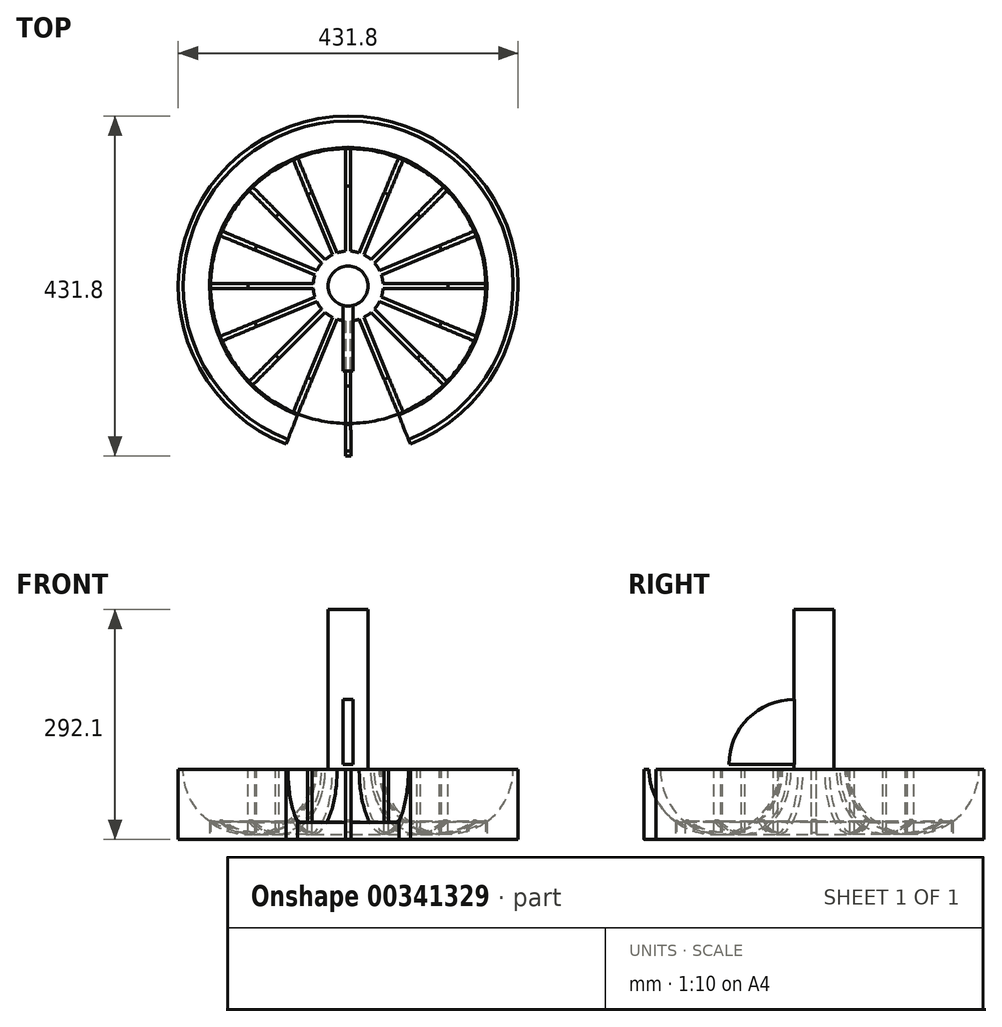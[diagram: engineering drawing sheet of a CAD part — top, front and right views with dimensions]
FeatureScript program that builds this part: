
annotation { "Feature Type Name" : "Feature", "Feature Type Description" : "" }
export const myFeature = defineFeature(function(context is Context, id is Id, definition is map)
    precondition{}
    {
        {
            var Q0;
            Q0=qCreatedBy(makeId("Front.planeOp"),FACE);
            var sketch = newSketch(context, id + "F0", { "sketchPlane" : qUnion([Q0])});
            skLineSegment(sketch, "E0.bottom", {"start": v(0, 0) * mm, "end": v(25.4, 0) * mm});
            skLineSegment(sketch, "E0.top", {"start": v(0, 292.1) * mm, "end": v(25.4, 292.1) * mm});
            skLineSegment(sketch, "E0.left", {"start": v(0, 0) * mm, "end": v(0, 292.1) * mm});
            skLineSegment(sketch, "E0.right", {"start": v(25.4, 88.9) * mm, "end": v(25.4, 292.1) * mm});
            skLineSegment(sketch, "E1.bottom", {"start": v(38.1, 0) * mm, "end": v(215.9, 0) * mm});
            skLineSegment(sketch, "E1.top", {"start": v(38.1, 88.9) * mm, "end": v(44.45, 88.9) * mm});
            skLineSegment(sketch, "E1.right", {"start": v(215.9, 0) * mm, "end": v(215.9, 88.9) * mm});
            skArc(sketch, "E2", {"start": v(209.55, 88.9) * mm, "mid": v(127, 6.35) * mm, "end": v(44.45, 88.9) * mm});
            skLineSegment(sketch, "E3", {"start": v(38.1, 88.9) * mm, "end": v(25.4, 88.9) * mm});
            skLineSegment(sketch, "E4", {"start": v(38.1, 0) * mm, "end": v(25.4, 0) * mm});
            skLineSegment(sketch, "E5.trimOffspring", {"start": v(209.55, 88.9) * mm, "end": v(215.9, 88.9) * mm});
            skSolve(sketch);
        }
        {
            var Q0;
            Q0=makeQuery(id+"F0.imprint","IMPRINT",FACE,{"disambiguationData":[TD([[makeQuery(id+"F0.imprint","IMPRINT",EDGE,{"derivedFrom":sQuery(id+"F0.wireOp",EDGE,"E0.bottom")}),1.0]])]});
            var Q1;
            Q1=sQuery(id+"F0.wireOp",EDGE,"E0.left");
            revolve(context, id + "F1", {"entities" : qUnion([Q0]), "axis" : qUnion([Q1]), "revolveType" : RevolveType.FULL});
        }
        {
            var Q0;
            Q0=qCreatedBy(makeId("Front.planeOp"),FACE);
            var sketch = newSketch(context, id + "F2", { "sketchPlane" : qUnion([Q0])});
            skLineSegment(sketch, "E6.bottom", {"start": v(0, 0) * mm, "end": v(127, 0) * mm, "construction": true});
            skLineSegment(sketch, "E6.top", {"start": v(0, 88.9) * mm, "end": v(127, 88.9) * mm, "construction": true});
            skLineSegment(sketch, "E6.left", {"start": v(0, 0) * mm, "end": v(0, 88.9) * mm, "construction": true});
            skLineSegment(sketch, "E6.right", {"start": v(127, 0) * mm, "end": v(127, 88.9) * mm, "construction": true});
            skArc(sketch, "E7", {"start": v(207.01, 88.9) * mm, "mid": v(127, 8.89) * mm, "end": v(46.99, 88.9) * mm});
            skArc(sketch, "E8", {"start": v(41.9, 88.9) * mm, "mid": v(127, 3.8) * mm, "end": v(212.1, 88.9) * mm});
            skLineSegment(sketch, "E9", {"start": v(41.9, 88.9) * mm, "end": v(46.99, 88.9) * mm});
            skLineSegment(sketch, "E10", {"start": v(207.01, 88.9) * mm, "end": v(212.1, 88.9) * mm});
            skLineSegment(sketch, "E11", {"start": v(46.99, 88.9) * mm, "end": v(127, 88.9) * mm});
            skLineSegment(sketch, "E12", {"start": v(127, 8.89) * mm, "end": v(127, 88.9) * mm});
            skSolve(sketch);
        }
        {
            var Q0;
            Q0 = qSketchRegion(id + "F2", true);
            extrude(context, id + "F3", {"entities" : qUnion([Q0]), "operationType" : NewBodyOperationType.ADD, "endBound" : BoundingType.SYMMETRIC, "depth" : 6.35 * mm});
        }
        {
            var Q0;
            Q0=makeQuery(id+"F1.opRevolve","SWEPT_BODY",BODY,{"disambiguationData":[OSD([sQuery(id+"F0.wireOp",EDGE,"E0.bottom"),sQuery(id+"F0.wireOp",EDGE,"E0.top"),sQuery(id+"F0.wireOp",EDGE,"E0.left"),sQuery(id+"F0.wireOp",EDGE,"E0.right"),sQuery(id+"F0.wireOp",EDGE,"E1.bottom"),sQuery(id+"F0.wireOp",EDGE,"E1.top"),sQuery(id+"F0.wireOp",EDGE,"E1.right"),sQuery(id+"F0.wireOp",EDGE,"E2"),sQuery(id+"F0.wireOp",EDGE,"E3"),sQuery(id+"F0.wireOp",EDGE,"E4"),sQuery(id+"F0.wireOp",EDGE,"E5.trimOffspring")])]});
            var Q1;
            Q1=makeQuery(id+"F1.opRevolve","SWEPT_FACE",FACE,{"disambiguationData":[OSD([sQuery(id+"F0.wireOp",EDGE,"E0.right")])]});
            circularPattern(context, id + "F4", {"entities" : qUnion([Q0]), "axis" : qUnion([Q1]), "angle" : 360 * degree, "instanceCount" : 16, "equalSpace" : true});
        }
        {
            var Q0;
            Q0=qCreatedBy(makeId("Right.planeOp"),FACE);
            var sketch = newSketch(context, id + "F5", { "sketchPlane" : qUnion([Q0])});
            skLineSegment(sketch, "E13", {"start": v(0, 0) * mm, "end": v(0, 232.3) * mm, "construction": true});
            skLineSegment(sketch, "E14", {"start": v(0, 232.3) * mm, "end": v(0, 0) * mm, "construction": true});
            skLineSegment(sketch, "E15", {"start": v(-25.4, 254.95) * mm, "end": v(-25.4, -56.78) * mm, "construction": true});
            skLineSegment(sketch, "E16", {"start": v(-25.4, 95.25) * mm, "end": v(-107.95, 95.25) * mm});
            skArc(sketch, "E17", {"start": v(-107.95, 95.25) * mm, "mid": v(-83.77, 153.62) * mm, "end": v(-25.4, 177.8) * mm});
            skLineSegment(sketch, "E18.bottom", {"start": v(-25.4, 95.25) * mm, "end": v(-12.7, 95.25) * mm});
            skLineSegment(sketch, "E18.top", {"start": v(-25.4, 177.8) * mm, "end": v(-12.7, 177.8) * mm});
            skLineSegment(sketch, "E18.left", {"start": v(-25.4, 95.25) * mm, "end": v(-25.4, 177.8) * mm});
            skLineSegment(sketch, "E18.right", {"start": v(-12.7, 95.25) * mm, "end": v(-12.7, 177.8) * mm});
            skSolve(sketch);
        }
        {
            var Q0;
            Q0 = qSketchRegion(id + "F5", true);
            extrude(context, id + "F6", {"entities" : qUnion([Q0]), "endBound" : BoundingType.SYMMETRIC, "depth" : 12.7 * mm});
        }
        {
            var Q0;
            Q0=makeQuery(id+"F4.opPattern","COPY",BODY,{"derivedFrom":makeQuery(id+"F1.opRevolve","SWEPT_BODY",BODY,{"disambiguationData":[OSD([sQuery(id+"F0.wireOp",EDGE,"E0.bottom"),sQuery(id+"F0.wireOp",EDGE,"E0.top"),sQuery(id+"F0.wireOp",EDGE,"E0.left"),sQuery(id+"F0.wireOp",EDGE,"E0.right"),sQuery(id+"F0.wireOp",EDGE,"E1.bottom"),sQuery(id+"F0.wireOp",EDGE,"E1.top"),sQuery(id+"F0.wireOp",EDGE,"E1.right"),sQuery(id+"F0.wireOp",EDGE,"E2"),sQuery(id+"F0.wireOp",EDGE,"E3"),sQuery(id+"F0.wireOp",EDGE,"E4"),sQuery(id+"F0.wireOp",EDGE,"E5.trimOffspring")])]}),"instanceName":"1"});
            var Q1;
            Q1=makeQuery(id+"F4.opPattern","COPY",BODY,{"derivedFrom":makeQuery(id+"F1.opRevolve","SWEPT_BODY",BODY,{"disambiguationData":[OSD([sQuery(id+"F0.wireOp",EDGE,"E0.bottom"),sQuery(id+"F0.wireOp",EDGE,"E0.top"),sQuery(id+"F0.wireOp",EDGE,"E0.left"),sQuery(id+"F0.wireOp",EDGE,"E0.right"),sQuery(id+"F0.wireOp",EDGE,"E1.bottom"),sQuery(id+"F0.wireOp",EDGE,"E1.top"),sQuery(id+"F0.wireOp",EDGE,"E1.right"),sQuery(id+"F0.wireOp",EDGE,"E2"),sQuery(id+"F0.wireOp",EDGE,"E3"),sQuery(id+"F0.wireOp",EDGE,"E4"),sQuery(id+"F0.wireOp",EDGE,"E5.trimOffspring")])]}),"instanceName":"2"});
            var Q2;
            Q2=makeQuery(id+"F4.opPattern","COPY",BODY,{"derivedFrom":makeQuery(id+"F1.opRevolve","SWEPT_BODY",BODY,{"disambiguationData":[OSD([sQuery(id+"F0.wireOp",EDGE,"E0.bottom"),sQuery(id+"F0.wireOp",EDGE,"E0.top"),sQuery(id+"F0.wireOp",EDGE,"E0.left"),sQuery(id+"F0.wireOp",EDGE,"E0.right"),sQuery(id+"F0.wireOp",EDGE,"E1.bottom"),sQuery(id+"F0.wireOp",EDGE,"E1.top"),sQuery(id+"F0.wireOp",EDGE,"E1.right"),sQuery(id+"F0.wireOp",EDGE,"E2"),sQuery(id+"F0.wireOp",EDGE,"E3"),sQuery(id+"F0.wireOp",EDGE,"E4"),sQuery(id+"F0.wireOp",EDGE,"E5.trimOffspring")])]}),"instanceName":"3"});
            var Q3;
            Q3=makeQuery(id+"F4.opPattern","COPY",BODY,{"derivedFrom":makeQuery(id+"F1.opRevolve","SWEPT_BODY",BODY,{"disambiguationData":[OSD([sQuery(id+"F0.wireOp",EDGE,"E0.bottom"),sQuery(id+"F0.wireOp",EDGE,"E0.top"),sQuery(id+"F0.wireOp",EDGE,"E0.left"),sQuery(id+"F0.wireOp",EDGE,"E0.right"),sQuery(id+"F0.wireOp",EDGE,"E1.bottom"),sQuery(id+"F0.wireOp",EDGE,"E1.top"),sQuery(id+"F0.wireOp",EDGE,"E1.right"),sQuery(id+"F0.wireOp",EDGE,"E2"),sQuery(id+"F0.wireOp",EDGE,"E3"),sQuery(id+"F0.wireOp",EDGE,"E4"),sQuery(id+"F0.wireOp",EDGE,"E5.trimOffspring")])]}),"instanceName":"7"});
            var Q4;
            Q4=makeQuery(id+"F4.opPattern","COPY",BODY,{"derivedFrom":makeQuery(id+"F1.opRevolve","SWEPT_BODY",BODY,{"disambiguationData":[OSD([sQuery(id+"F0.wireOp",EDGE,"E0.bottom"),sQuery(id+"F0.wireOp",EDGE,"E0.top"),sQuery(id+"F0.wireOp",EDGE,"E0.left"),sQuery(id+"F0.wireOp",EDGE,"E0.right"),sQuery(id+"F0.wireOp",EDGE,"E1.bottom"),sQuery(id+"F0.wireOp",EDGE,"E1.top"),sQuery(id+"F0.wireOp",EDGE,"E1.right"),sQuery(id+"F0.wireOp",EDGE,"E2"),sQuery(id+"F0.wireOp",EDGE,"E3"),sQuery(id+"F0.wireOp",EDGE,"E4"),sQuery(id+"F0.wireOp",EDGE,"E5.trimOffspring")])]}),"instanceName":"4"});
            var Q5;
            Q5=makeQuery(id+"F4.opPattern","COPY",BODY,{"derivedFrom":makeQuery(id+"F1.opRevolve","SWEPT_BODY",BODY,{"disambiguationData":[OSD([sQuery(id+"F0.wireOp",EDGE,"E0.bottom"),sQuery(id+"F0.wireOp",EDGE,"E0.top"),sQuery(id+"F0.wireOp",EDGE,"E0.left"),sQuery(id+"F0.wireOp",EDGE,"E0.right"),sQuery(id+"F0.wireOp",EDGE,"E1.bottom"),sQuery(id+"F0.wireOp",EDGE,"E1.top"),sQuery(id+"F0.wireOp",EDGE,"E1.right"),sQuery(id+"F0.wireOp",EDGE,"E2"),sQuery(id+"F0.wireOp",EDGE,"E3"),sQuery(id+"F0.wireOp",EDGE,"E4"),sQuery(id+"F0.wireOp",EDGE,"E5.trimOffspring")])]}),"instanceName":"5"});
            var Q6;
            Q6=makeQuery(id+"F4.opPattern","COPY",BODY,{"derivedFrom":makeQuery(id+"F1.opRevolve","SWEPT_BODY",BODY,{"disambiguationData":[OSD([sQuery(id+"F0.wireOp",EDGE,"E0.bottom"),sQuery(id+"F0.wireOp",EDGE,"E0.top"),sQuery(id+"F0.wireOp",EDGE,"E0.left"),sQuery(id+"F0.wireOp",EDGE,"E0.right"),sQuery(id+"F0.wireOp",EDGE,"E1.bottom"),sQuery(id+"F0.wireOp",EDGE,"E1.top"),sQuery(id+"F0.wireOp",EDGE,"E1.right"),sQuery(id+"F0.wireOp",EDGE,"E2"),sQuery(id+"F0.wireOp",EDGE,"E3"),sQuery(id+"F0.wireOp",EDGE,"E4"),sQuery(id+"F0.wireOp",EDGE,"E5.trimOffspring")])]}),"instanceName":"12"});
            var Q7;
            Q7=makeQuery(id+"F4.opPattern","COPY",BODY,{"derivedFrom":makeQuery(id+"F1.opRevolve","SWEPT_BODY",BODY,{"disambiguationData":[OSD([sQuery(id+"F0.wireOp",EDGE,"E0.bottom"),sQuery(id+"F0.wireOp",EDGE,"E0.top"),sQuery(id+"F0.wireOp",EDGE,"E0.left"),sQuery(id+"F0.wireOp",EDGE,"E0.right"),sQuery(id+"F0.wireOp",EDGE,"E1.bottom"),sQuery(id+"F0.wireOp",EDGE,"E1.top"),sQuery(id+"F0.wireOp",EDGE,"E1.right"),sQuery(id+"F0.wireOp",EDGE,"E2"),sQuery(id+"F0.wireOp",EDGE,"E3"),sQuery(id+"F0.wireOp",EDGE,"E4"),sQuery(id+"F0.wireOp",EDGE,"E5.trimOffspring")])]}),"instanceName":"9"});
            var Q8;
            Q8=makeQuery(id+"F4.opPattern","COPY",BODY,{"derivedFrom":makeQuery(id+"F1.opRevolve","SWEPT_BODY",BODY,{"disambiguationData":[OSD([sQuery(id+"F0.wireOp",EDGE,"E0.bottom"),sQuery(id+"F0.wireOp",EDGE,"E0.top"),sQuery(id+"F0.wireOp",EDGE,"E0.left"),sQuery(id+"F0.wireOp",EDGE,"E0.right"),sQuery(id+"F0.wireOp",EDGE,"E1.bottom"),sQuery(id+"F0.wireOp",EDGE,"E1.top"),sQuery(id+"F0.wireOp",EDGE,"E1.right"),sQuery(id+"F0.wireOp",EDGE,"E2"),sQuery(id+"F0.wireOp",EDGE,"E3"),sQuery(id+"F0.wireOp",EDGE,"E4"),sQuery(id+"F0.wireOp",EDGE,"E5.trimOffspring")])]}),"instanceName":"10"});
            var Q9;
            Q9=makeQuery(id+"F6.opExtrude","SWEPT_BODY",BODY,{"disambiguationData":[OSD([sQuery(id+"F5.wireOp",EDGE,"E16"),sQuery(id+"F5.wireOp",EDGE,"E17"),sQuery(id+"F5.wireOp",EDGE,"E18.bottom"),sQuery(id+"F5.wireOp",EDGE,"E18.top"),sQuery(id+"F5.wireOp",EDGE,"E18.right")])]});
            var Q10;
            Q10=makeQuery(id+"F4.opPattern","COPY",BODY,{"derivedFrom":makeQuery(id+"F1.opRevolve","SWEPT_BODY",BODY,{"disambiguationData":[OSD([sQuery(id+"F0.wireOp",EDGE,"E0.bottom"),sQuery(id+"F0.wireOp",EDGE,"E0.top"),sQuery(id+"F0.wireOp",EDGE,"E0.left"),sQuery(id+"F0.wireOp",EDGE,"E0.right"),sQuery(id+"F0.wireOp",EDGE,"E1.bottom"),sQuery(id+"F0.wireOp",EDGE,"E1.top"),sQuery(id+"F0.wireOp",EDGE,"E1.right"),sQuery(id+"F0.wireOp",EDGE,"E2"),sQuery(id+"F0.wireOp",EDGE,"E3"),sQuery(id+"F0.wireOp",EDGE,"E4"),sQuery(id+"F0.wireOp",EDGE,"E5.trimOffspring")])]}),"instanceName":"15"});
            var Q11;
            Q11=makeQuery(id+"F4.opPattern","COPY",BODY,{"derivedFrom":makeQuery(id+"F1.opRevolve","SWEPT_BODY",BODY,{"disambiguationData":[OSD([sQuery(id+"F0.wireOp",EDGE,"E0.bottom"),sQuery(id+"F0.wireOp",EDGE,"E0.top"),sQuery(id+"F0.wireOp",EDGE,"E0.left"),sQuery(id+"F0.wireOp",EDGE,"E0.right"),sQuery(id+"F0.wireOp",EDGE,"E1.bottom"),sQuery(id+"F0.wireOp",EDGE,"E1.top"),sQuery(id+"F0.wireOp",EDGE,"E1.right"),sQuery(id+"F0.wireOp",EDGE,"E2"),sQuery(id+"F0.wireOp",EDGE,"E3"),sQuery(id+"F0.wireOp",EDGE,"E4"),sQuery(id+"F0.wireOp",EDGE,"E5.trimOffspring")])]}),"instanceName":"8"});
            var Q12;
            Q12=makeQuery(id+"F4.opPattern","COPY",BODY,{"derivedFrom":makeQuery(id+"F1.opRevolve","SWEPT_BODY",BODY,{"disambiguationData":[OSD([sQuery(id+"F0.wireOp",EDGE,"E0.bottom"),sQuery(id+"F0.wireOp",EDGE,"E0.top"),sQuery(id+"F0.wireOp",EDGE,"E0.left"),sQuery(id+"F0.wireOp",EDGE,"E0.right"),sQuery(id+"F0.wireOp",EDGE,"E1.bottom"),sQuery(id+"F0.wireOp",EDGE,"E1.top"),sQuery(id+"F0.wireOp",EDGE,"E1.right"),sQuery(id+"F0.wireOp",EDGE,"E2"),sQuery(id+"F0.wireOp",EDGE,"E3"),sQuery(id+"F0.wireOp",EDGE,"E4"),sQuery(id+"F0.wireOp",EDGE,"E5.trimOffspring")])]}),"instanceName":"11"});
            var Q13;
            Q13=makeQuery(id+"F4.opPattern","COPY",BODY,{"derivedFrom":makeQuery(id+"F1.opRevolve","SWEPT_BODY",BODY,{"disambiguationData":[OSD([sQuery(id+"F0.wireOp",EDGE,"E0.bottom"),sQuery(id+"F0.wireOp",EDGE,"E0.top"),sQuery(id+"F0.wireOp",EDGE,"E0.left"),sQuery(id+"F0.wireOp",EDGE,"E0.right"),sQuery(id+"F0.wireOp",EDGE,"E1.bottom"),sQuery(id+"F0.wireOp",EDGE,"E1.top"),sQuery(id+"F0.wireOp",EDGE,"E1.right"),sQuery(id+"F0.wireOp",EDGE,"E2"),sQuery(id+"F0.wireOp",EDGE,"E3"),sQuery(id+"F0.wireOp",EDGE,"E4"),sQuery(id+"F0.wireOp",EDGE,"E5.trimOffspring")])]}),"instanceName":"14"});
            var Q14;
            Q14=makeQuery(id+"F4.opPattern","COPY",BODY,{"derivedFrom":makeQuery(id+"F1.opRevolve","SWEPT_BODY",BODY,{"disambiguationData":[OSD([sQuery(id+"F0.wireOp",EDGE,"E0.bottom"),sQuery(id+"F0.wireOp",EDGE,"E0.top"),sQuery(id+"F0.wireOp",EDGE,"E0.left"),sQuery(id+"F0.wireOp",EDGE,"E0.right"),sQuery(id+"F0.wireOp",EDGE,"E1.bottom"),sQuery(id+"F0.wireOp",EDGE,"E1.top"),sQuery(id+"F0.wireOp",EDGE,"E1.right"),sQuery(id+"F0.wireOp",EDGE,"E2"),sQuery(id+"F0.wireOp",EDGE,"E3"),sQuery(id+"F0.wireOp",EDGE,"E4"),sQuery(id+"F0.wireOp",EDGE,"E5.trimOffspring")])]}),"instanceName":"13"});
            var Q15;
            Q15=makeQuery(id+"F4.opPattern","COPY",BODY,{"derivedFrom":makeQuery(id+"F1.opRevolve","SWEPT_BODY",BODY,{"disambiguationData":[OSD([sQuery(id+"F0.wireOp",EDGE,"E0.bottom"),sQuery(id+"F0.wireOp",EDGE,"E0.top"),sQuery(id+"F0.wireOp",EDGE,"E0.left"),sQuery(id+"F0.wireOp",EDGE,"E0.right"),sQuery(id+"F0.wireOp",EDGE,"E1.bottom"),sQuery(id+"F0.wireOp",EDGE,"E1.top"),sQuery(id+"F0.wireOp",EDGE,"E1.right"),sQuery(id+"F0.wireOp",EDGE,"E2"),sQuery(id+"F0.wireOp",EDGE,"E3"),sQuery(id+"F0.wireOp",EDGE,"E4"),sQuery(id+"F0.wireOp",EDGE,"E5.trimOffspring")])]}),"instanceName":"6"});
            booleanBodies(context, id + "F7", {"operationType" : BooleanOperationType.UNION, "tools" : qUnion([Q0, Q1, Q2, Q3, Q4, Q5, Q6, Q7, Q8, Q9, Q10, Q11, Q12, Q13, Q14, Q15])});
        }
        {
            var Q0;
            Q0=makeQuery(id+"F1.opRevolve","SWEPT_BODY",BODY,{"disambiguationData":[OSD([sQuery(id+"F0.wireOp",EDGE,"E0.bottom"),sQuery(id+"F0.wireOp",EDGE,"E0.top"),sQuery(id+"F0.wireOp",EDGE,"E0.left"),sQuery(id+"F0.wireOp",EDGE,"E0.right"),sQuery(id+"F0.wireOp",EDGE,"E1.bottom"),sQuery(id+"F0.wireOp",EDGE,"E1.top"),sQuery(id+"F0.wireOp",EDGE,"E1.right"),sQuery(id+"F0.wireOp",EDGE,"E2"),sQuery(id+"F0.wireOp",EDGE,"E3"),sQuery(id+"F0.wireOp",EDGE,"E4"),sQuery(id+"F0.wireOp",EDGE,"E5.trimOffspring")])]});
            var Q1;
            Q1=makeQuery(id+"F4.opPattern","COPY",BODY,{"derivedFrom":makeQuery(id+"F1.opRevolve","SWEPT_BODY",BODY,{"disambiguationData":[OSD([sQuery(id+"F0.wireOp",EDGE,"E0.bottom"),sQuery(id+"F0.wireOp",EDGE,"E0.top"),sQuery(id+"F0.wireOp",EDGE,"E0.left"),sQuery(id+"F0.wireOp",EDGE,"E0.right"),sQuery(id+"F0.wireOp",EDGE,"E1.bottom"),sQuery(id+"F0.wireOp",EDGE,"E1.top"),sQuery(id+"F0.wireOp",EDGE,"E1.right"),sQuery(id+"F0.wireOp",EDGE,"E2"),sQuery(id+"F0.wireOp",EDGE,"E3"),sQuery(id+"F0.wireOp",EDGE,"E4"),sQuery(id+"F0.wireOp",EDGE,"E5.trimOffspring")])]}),"instanceName":"1"});
            booleanBodies(context, id + "F8", {"operationType" : BooleanOperationType.UNION, "tools" : qUnion([Q0, Q1])});
        }
        {
            var Q0;
            Q0=qCreatedBy(makeId("Top.planeOp"),FACE);
            var sketch = newSketch(context, id + "F9", { "sketchPlane" : qUnion([Q0])});
            skCircle(sketch, "E19", {"center": v(0, 0) * mm, "radius": 174.63 * mm});
            skCircle(sketch, "E20", {"center": v(0, 0) * mm, "radius": 176.21 * mm});
            skSolve(sketch);
        }
        {
            var Q0;
            Q0 = qSketchRegion(id + "F9", true);
            extrude(context, id + "F10", {"entities" : qUnion([Q0]), "operationType" : NewBodyOperationType.REMOVE, "endBound" : BoundingType.THROUGH_ALL, "depth" : 25.4 * mm});
        }
        {
            var Q0;
            Q0=qCreatedBy(makeId("Front.planeOp"),FACE);
            var sketch = newSketch(context, id + "F11", { "sketchPlane" : qUnion([Q0])});
            skLineSegment(sketch, "E21.bottom", {"start": v(0, 0) * mm, "end": v(127, 0) * mm, "construction": true});
            skLineSegment(sketch, "E21.top", {"start": v(0, 88.9) * mm, "end": v(127, 88.9) * mm, "construction": true});
            skLineSegment(sketch, "E21.left", {"start": v(0, 0) * mm, "end": v(0, 88.9) * mm, "construction": true});
            skLineSegment(sketch, "E21.right", {"start": v(127, 0) * mm, "end": v(127, 88.9) * mm, "construction": true});
            skArc(sketch, "E22", {"start": v(176.14, 22.57) * mm, "mid": v(200.73, 51.77) * mm, "end": v(209.55, 88.9) * mm});
            skArc(sketch, "E23", {"start": v(173.8, 28.76) * mm, "mid": v(195.46, 55.43) * mm, "end": v(203.2, 88.9) * mm});
            skLineSegment(sketch, "E24", {"start": v(203.2, 88.9) * mm, "end": v(209.55, 88.9) * mm});
            skLineSegment(sketch, "E25", {"start": v(173.8, 28.76) * mm, "end": v(176.14, 22.57) * mm});
            skSolve(sketch);
        }
        {
            var Q0;
            Q0 = qSketchRegion(id + "F11", true);
            var Q1;
            Q1=makeQuery(id+"F1.opRevolve","SWEPT_EDGE",EDGE,{"disambiguationData":[OSD([sQuery(id+"F0.wireOp",EDGE,"E0.top"),sQuery(id+"F0.wireOp",EDGE,"E0.right")])]});
            revolve(context, id + "F12", {"operationType" : NewBodyOperationType.REMOVE, "entities" : qUnion([Q0]), "axis" : qUnion([Q1]), "revolveType" : RevolveType.FULL, "oppositeDirection" : true});
        }
        {
            var Q0;
            {var subQ0=makeQuery(id+"F3.boolean.opBoolean","MERGE",FACE,{"derivedFrom":[makeQuery(id+"F1.opRevolve","SWEPT_FACE",FACE,{"disambiguationData":[OSD([sQuery(id+"F0.wireOp",EDGE,"E5.trimOffspring")])]}),makeQuery(id+"F3.opExtrude","SWEPT_FACE",FACE,{"disambiguationData":[OSD([sQuery(id+"F2.wireOp",EDGE,"E10")])]})]});Q0=makeQuery(id+"F8.opBoolean","MERGE",FACE,{"derivedFrom":[subQ0,makeQuery(id+"F7.opBoolean","MERGE",FACE,{"derivedFrom":[makeQuery(id+"F4.opPattern","COPY",FACE,{"derivedFrom":subQ0,"instanceName":"1"}),makeQuery(id+"F4.opPattern","COPY",FACE,{"derivedFrom":subQ0,"instanceName":"2"}),makeQuery(id+"F4.opPattern","COPY",FACE,{"derivedFrom":subQ0,"instanceName":"3"}),makeQuery(id+"F4.opPattern","COPY",FACE,{"derivedFrom":subQ0,"instanceName":"4"}),makeQuery(id+"F4.opPattern","COPY",FACE,{"derivedFrom":subQ0,"instanceName":"5"}),makeQuery(id+"F4.opPattern","COPY",FACE,{"derivedFrom":subQ0,"instanceName":"6"}),makeQuery(id+"F4.opPattern","COPY",FACE,{"derivedFrom":subQ0,"instanceName":"7"}),makeQuery(id+"F4.opPattern","COPY",FACE,{"derivedFrom":subQ0,"instanceName":"8"}),makeQuery(id+"F4.opPattern","COPY",FACE,{"derivedFrom":subQ0,"instanceName":"9"}),makeQuery(id+"F4.opPattern","COPY",FACE,{"derivedFrom":subQ0,"instanceName":"10"}),makeQuery(id+"F4.opPattern","COPY",FACE,{"derivedFrom":subQ0,"instanceName":"11"}),makeQuery(id+"F4.opPattern","COPY",FACE,{"derivedFrom":subQ0,"instanceName":"12"}),makeQuery(id+"F4.opPattern","COPY",FACE,{"derivedFrom":subQ0,"instanceName":"13"}),makeQuery(id+"F4.opPattern","COPY",FACE,{"derivedFrom":subQ0,"instanceName":"14"}),makeQuery(id+"F4.opPattern","COPY",FACE,{"derivedFrom":subQ0,"instanceName":"15"})]})]});}
            var sketch = newSketch(context, id + "F13", { "sketchPlane" : qUnion([Q0])});
            skArc(sketch, "E26", {"start": v(64.08, -163.2) * mm, "mid": v(34.19, -171.97) * mm, "end": v(3.22, -175.3) * mm});
            skArc(sketch, "E27", {"start": v(78.93, -200.96) * mm, "mid": v(42.04, -211.77) * mm, "end": v(3.81, -215.87) * mm});
            skLineSegment(sketch, "E28", {"start": v(64.08, -163.2) * mm, "end": v(78.93, -200.96) * mm});
            skLineSegment(sketch, "E29", {"start": v(-63.98, -163.24) * mm, "end": v(-78.96, -200.94) * mm});
            skLineSegment(sketch, "E30", {"start": v(3.22, -175.3) * mm, "end": v(3.81, -215.87) * mm});
            skLineSegment(sketch, "E31", {"start": v(-3.29, -175.3) * mm, "end": v(-3.29, -215.87) * mm});
            skArc(sketch, "E32.trimOffspring", {"start": v(-3.29, -175.3) * mm, "mid": v(-34.17, -171.97) * mm, "end": v(-63.98, -163.24) * mm});
            skArc(sketch, "E33.trimOffspring", {"start": v(-3.29, -215.87) * mm, "mid": v(-41.8, -211.82) * mm, "end": v(-78.96, -200.94) * mm});
            skSolve(sketch);
        }
        {
            var Q0;
            Q0 = qSketchRegion(id + "F13", true);
            extrude(context, id + "F14", {"entities" : qUnion([Q0]), "operationType" : NewBodyOperationType.REMOVE, "endBound" : BoundingType.THROUGH_ALL, "oppositeDirection" : true, "depth" : 25.4 * mm});
        }
    });
